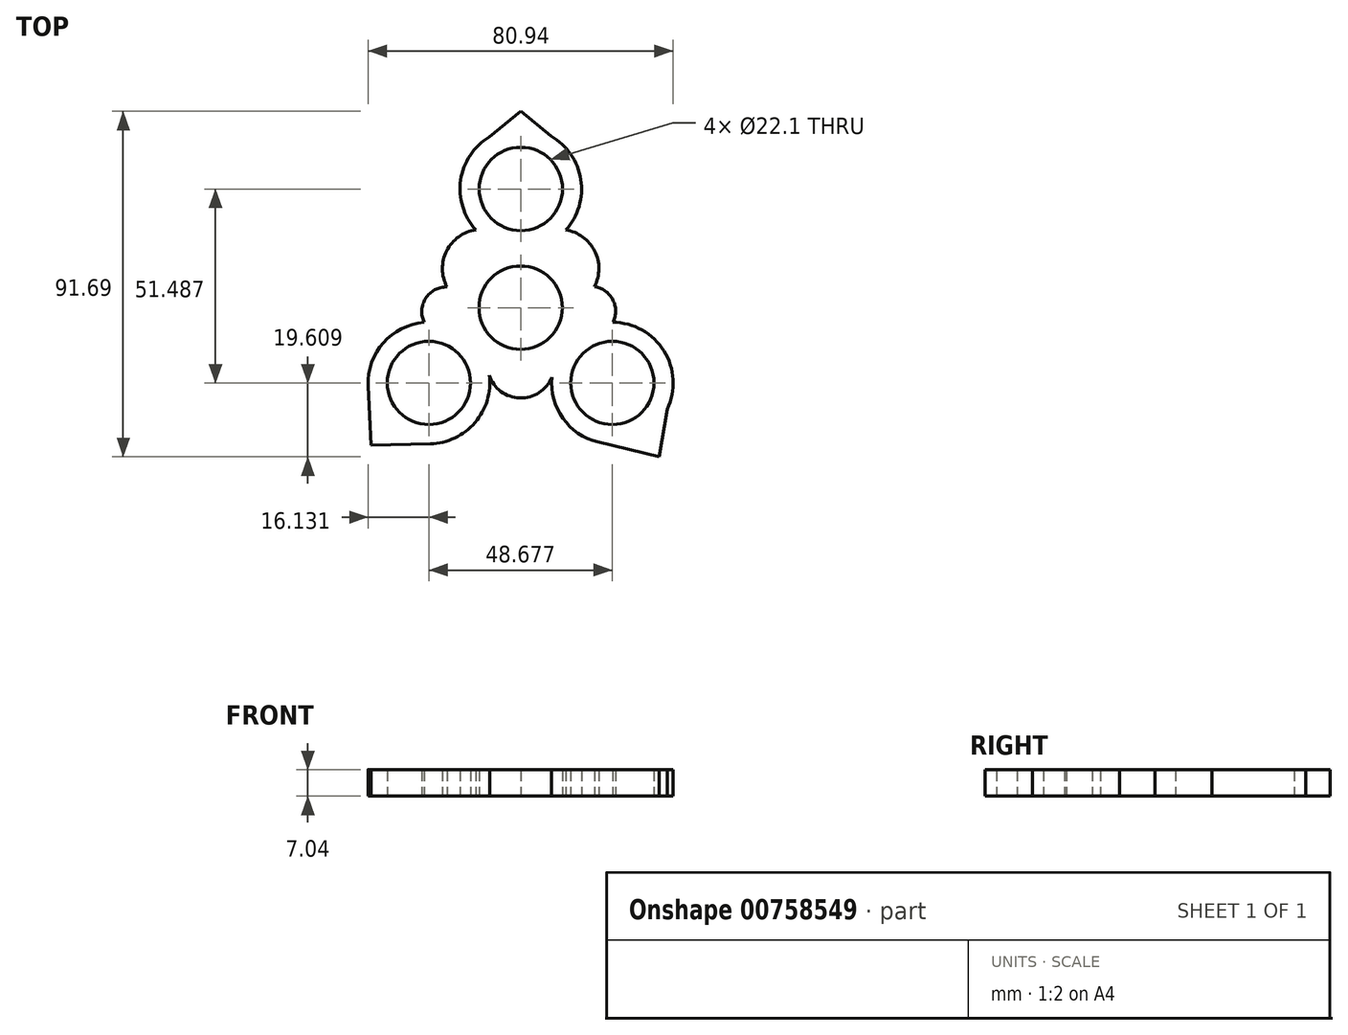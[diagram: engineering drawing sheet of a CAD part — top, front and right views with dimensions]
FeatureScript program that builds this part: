
annotation { "Feature Type Name" : "Feature", "Feature Type Description" : "" }
export const myFeature = defineFeature(function(context is Context, id is Id, definition is map)
    precondition{}
    {
        {
            var Q0;
            Q0=qCreatedBy(makeId("Top.planeOp"),FACE);
            var sketch = newSketch(context, id + "F0", { "sketchPlane" : qUnion([Q0])});
            skCircle(sketch, "E0", {"center": v(0.05, 31.5) * mm, "radius": 11.05 * mm});
            skCircle(sketch, "E1", {"center": v(0, 0) * mm, "radius": 11.05 * mm});
            skCircle(sketch, "E2", {"center": v(-24.34, -20) * mm, "radius": 11.05 * mm});
            skCircle(sketch, "E3", {"center": v(24.34, -20) * mm, "radius": 11.05 * mm});
            skCircle(sketch, "E4", {"center": v(0.05, 31.5) * mm, "radius": 16.13 * mm});
            skCircle(sketch, "E5", {"center": v(24.34, -20) * mm, "radius": 16.13 * mm});
            skCircle(sketch, "E6", {"center": v(-24.34, -20) * mm, "radius": 16.13 * mm});
            skLineSegment(sketch, "E7", {"start": v(0, 52.09) * mm, "end": v(-8.33, 45.28) * mm});
            skLineSegment(sketch, "E8.MirrorCS", {"start": v(0, 52.09) * mm, "end": v(8.33, 45.28) * mm});
            skLineSegment(sketch, "E9", {"start": v(-23.96, -36.12) * mm, "end": v(-39.72, -36.48) * mm});
            skLineSegment(sketch, "E10", {"start": v(-39.72, -36.48) * mm, "end": v(-40.45, -20.74) * mm});
            skLineSegment(sketch, "E11", {"start": v(20.53, -35.66) * mm, "end": v(36.72, -39.6) * mm});
            skLineSegment(sketch, "E12", {"start": v(36.72, -39.6) * mm, "end": v(38.89, -26.96) * mm});
            skArc(sketch, "E13", {"start": v(11.05, 0) * mm, "mid": v(17.72, 17.72) * mm, "end": v(0, 11.05) * mm});
            skArc(sketch, "E14", {"start": v(0, -11.05) * mm, "mid": v(13, -13) * mm, "end": v(11.05, 0) * mm});
            skArc(sketch, "E15", {"start": v(-11.05, 0) * mm, "mid": v(-13.43, -13.43) * mm, "end": v(0, -11.05) * mm});
            skArc(sketch, "E16", {"start": v(0, 11.05) * mm, "mid": v(-17.72, 17.72) * mm, "end": v(-11.05, 0) * mm});
            skArc(sketch, "E17", {"start": v(-19.55, 5.5) * mm, "mid": v(-25.93, -3.05) * mm, "end": v(-15.78, -6.32) * mm});
            skArc(sketch, "E18", {"start": v(15.36, -6.6) * mm, "mid": v(24.83, -3.07) * mm, "end": v(19.6, 5.58) * mm});
            skArc(sketch, "E19", {"start": v(-8.77, -15.78) * mm, "mid": v(0.36, -23.99) * mm, "end": v(8.94, -15.2) * mm});
            skArc(sketch, "E20", {"start": v(2.15, 16.73) * mm, "mid": v(-0.03, 18.98) * mm, "end": v(-2.02, 16.56) * mm});
            skSolve(sketch);
        }
        {
            var Q0;
            Q0 = qSketchRegion(id + "F0", true);
            var Q1;
            {var subQ0=sQuery(id+"F0.wireOp",EDGE,"E15");var subQ1=sQuery(id+"F0.wireOp",EDGE,"E6");var subQ2=makeQuery(id+"F0.imprint","INTERSECT",VERTEX,{"derivedFrom":[subQ1,subQ0,sQuery(id+"F0.wireOp",EDGE,"E17")]});Q1=makeQuery(id+"F0.imprint","IMPRINT",FACE,{"disambiguationData":[TD([[makeQuery(id+"F0.imprint","IMPRINT",EDGE,{"disambiguationData":[TD([[subQ2,1.0]])],"derivedFrom":subQ1}),1.0]])]});}
            var Q2;
            {var subQ0=sQuery(id+"F0.wireOp",EDGE,"E15");var subQ1=sQuery(id+"F0.wireOp",EDGE,"E1");var subQ2=makeQuery(id+"F0.imprint","INTERSECT",VERTEX,{"derivedFrom":[subQ1,sQuery(id+"F0.wireOp",EDGE,"E14"),subQ0]});Q2=makeQuery(id+"F0.imprint","IMPRINT",FACE,{"disambiguationData":[TD([[makeQuery(id+"F0.imprint","IMPRINT",EDGE,{"disambiguationData":[TD([[subQ2,1.0]])],"derivedFrom":subQ1}),-1.0]])]});}
            var Q3;
            {var subQ0=sQuery(id+"F0.wireOp",EDGE,"E14");var subQ1=sQuery(id+"F0.wireOp",EDGE,"E1");var subQ2=makeQuery(id+"F0.imprint","INTERSECT",VERTEX,{"derivedFrom":[subQ1,sQuery(id+"F0.wireOp",EDGE,"E13"),subQ0]});Q3=makeQuery(id+"F0.imprint","IMPRINT",FACE,{"disambiguationData":[TD([[makeQuery(id+"F0.imprint","IMPRINT",EDGE,{"disambiguationData":[TD([[subQ2,1.0]])],"derivedFrom":subQ1}),-1.0]])]});}
            var Q4;
            {var subQ0=sQuery(id+"F0.wireOp",EDGE,"E14");var subQ1=sQuery(id+"F0.wireOp",EDGE,"E5");var subQ2=makeQuery(id+"F0.imprint","INTERSECT",VERTEX,{"derivedFrom":[subQ1,subQ0,sQuery(id+"F0.wireOp",EDGE,"E18")]});Q4=makeQuery(id+"F0.imprint","IMPRINT",FACE,{"disambiguationData":[TD([[makeQuery(id+"F0.imprint","IMPRINT",EDGE,{"disambiguationData":[TD([[subQ2,-1.0]])],"derivedFrom":subQ1}),1.0]])]});}
            var Q5;
            {var subQ5=sQuery(id+"F0.wireOp",EDGE,"E20");Q5=makeQuery(id+"F0.imprint","IMPRINT",FACE,{"disambiguationData":[TD([[makeQuery(id+"F0.imprint","IMPRINT",EDGE,{"derivedFrom":subQ5}),1.0]])]});}
            var Q6;
            {var subQ0=sQuery(id+"F0.wireOp",EDGE,"E16");var subQ1=sQuery(id+"F0.wireOp",EDGE,"E4");var subQ2=makeQuery(id+"F0.imprint","INTERSECT",VERTEX,{"disambiguationData":[OD(1.0)],"derivedFrom":[subQ1,subQ0]});Q6=makeQuery(id+"F0.imprint","IMPRINT",FACE,{"disambiguationData":[TD([[makeQuery(id+"F0.imprint","IMPRINT",EDGE,{"disambiguationData":[TD([[subQ2,-1.0]])],"derivedFrom":subQ1}),-1.0]])]});}
            extrude(context, id + "F1", {"entities" : qUnion([Q0, Q1, Q2, Q3, Q4, Q5, Q6]), "depth" : 7.04 * mm, "offsetDistance" : 25.4 * mm});
        }
    });
